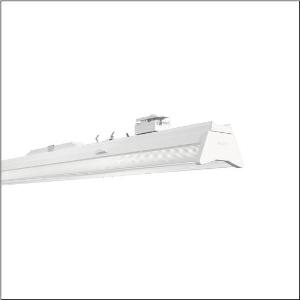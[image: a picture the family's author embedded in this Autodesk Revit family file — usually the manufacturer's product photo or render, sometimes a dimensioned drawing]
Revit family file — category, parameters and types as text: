
# Revit family: licross_r__21_performance_mo_52td16vn48xg_2cf7
name_source: partatom
category: Lighting Fixtures
units: mm (PartAtom-declared; Revit-internal decimal feet)

## family parameters
Cut with Voids When Loaded = No
Host = Face
Light Source = No
Part Type = Normal
Room Calculation Point = No
Round Connector Dimension = Use Diameter
Shared = No

## types (1)
- --- (1 x LED, 8000 lm, 44.6 W, 4000K)
    Apparent Load = 45 VA
    CIE Flux Codes = 66 88 96 79 100
    Color Rendering = 80
    Color Temperature = 4000K
    Default Elevation = 1800 mm
    Description = Licross® 21 Performance MO, luminaire insert, of sheet steel, galvanised, coil coated, white, length: 1.500mm, width: 120mm, height: 123mm, LED rated luminous flux: 8.000lm, light colour: 840, SDCM (Standard Deviation of Colour Matching)MacAdam ≤ 3 SDCM (initial), control gear: DALI 2, CLO, with plug, 5-pole, with phase selection, mains connection: 220..240V, AC, 50/60Hz, start of lifetime: 45W, end of service life: 53W, internal wiring halogen-free, primary light control with lens, of plastic, primary optical cover: cover, of PMMA, light emission: direct/indirect distribution, primary light characteristic: symmetric, protection rating (complete): IP54, insulation class (complete): insulation class I (protective earthing), certification: CE, ENEC, VDE, UKCA, protection symbol: D if used in an environment with non-conductive dust loads with corresponding accessories, impact resistance: IK06, permissible ambient temperature for indoor applications: -25..+45°C, corresponds to IFS (International Featured Standards) requirements for safety and quality in the food industry, reducing of maximum allowable ambient temperature of 5°C with ceiling mounting, LABS conformity tested according to VDMA 24364:2018-05, packaging unit: 1 piece
    Height = 114 mm
    Lamp = 1 x LED
    Lamp Light Flux = 8000 lm
    Lamp Power = 44.6 W
    Lamp count = 1
    Length = 1500 mm
    Luminous efficacy = 179 lm/W
    Manufacturer = Siteco
    ModVariant = No
    Model = 52TD16VN48XG
    Mounting Place = Ceiling
    Mounting Type = Pendant
    Number of Poles = 1
    OnlyDefault = Yes
    Power Factor = 1
    Product Name = Licross® 21 Performance MO
    Product group = luminaire insert | ceiling pendant
    ProductGroupID = 901
    Protection Class = Protection class I
    Protection Degree = IP 54
    RLX_Detail_Level = 1
    RLX_Emergency_Light_Flux = 0 lm
    RLX_Emergency_Type = 0
    RLX_Emergency_Type_DB = No
    RlxData = <blob elided: 34205 chars, md5=4820e6af>
    Socket = socket
    Standby Power = 0 W
    System Light Flux = 8000 lm
    System Power = 45 W
    Type Comments = factory setting: luminous flux: 100 % | dim-lin: 254 | 301 mA
    Type Image = l_1256138.jpg
    URL = http://relux.com
    VarID = @adj_090749
    Voltage = 0 V
    Weight = 0.00 kg
    Width = 120 mm

## geometry (parser evidence)
native form markers: Blend x4, Sweep x12
no freeform markers — native parametric forms only
